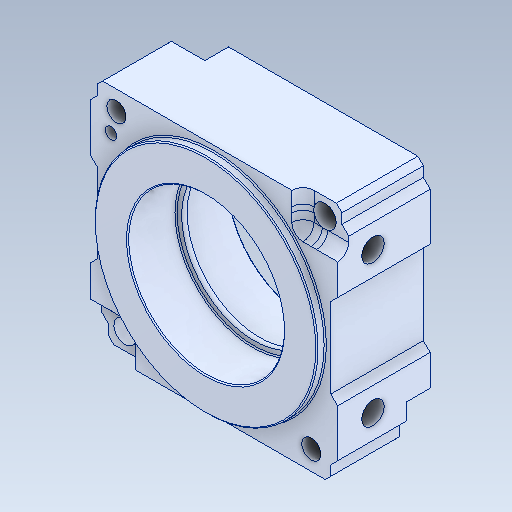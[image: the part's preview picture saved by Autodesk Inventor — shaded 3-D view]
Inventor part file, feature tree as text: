
AUTODESK INVENTOR PART (.ipt)
format: ipt  version: 2020 (Build 240168000, 168)  size: 261,120 bytes
history: native  units: in
note: dims shown in document units (in); Inventor stores cm internally (conversion verified against a paired STEP export)
features: chamfer x1
ambient origin geometry x8: Origin, YZ Plane, XZ Plane, XY Plane, X Axis, Y Axis, Z Axis, Center Point
bodies: Solid1 (feature_tree)
feature tree (1):
  chamfer  "Chamfer2"  [1 undecoded]
note: 1 required parameter value undecoded (feature->parameter linkage not recoverable at this tier; creation-order binding heuristic only, values carry confidence <= 0.55)
